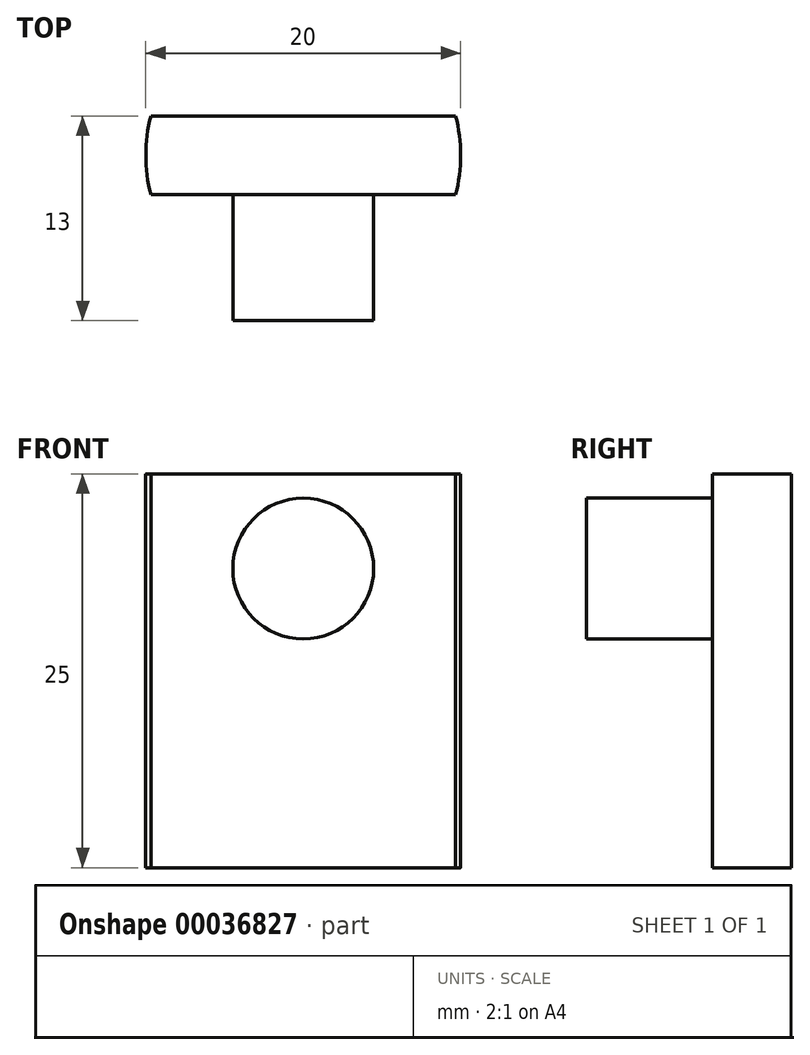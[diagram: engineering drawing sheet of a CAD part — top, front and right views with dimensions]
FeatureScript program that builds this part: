
annotation { "Feature Type Name" : "Feature", "Feature Type Description" : "" }
export const myFeature = defineFeature(function(context is Context, id is Id, definition is map)
    precondition{}
    {
        {
            var Q0;
            Q0=qCreatedBy(makeId("Top.planeOp"),FACE);
            var sketch = newSketch(context, id + "F0", { "sketchPlane" : qUnion([Q0])});
            skCircle(sketch, "E0", {"center": v(0, 0) * mm, "radius": 10 * mm});
            skLineSegment(sketch, "E1.rect.bottom", {"start": v(9.68, -2.5) * mm, "end": v(-9.68, -2.5) * mm});
            skLineSegment(sketch, "E1.rect.top", {"start": v(9.68, 2.5) * mm, "end": v(-9.68, 2.5) * mm});
            skSolve(sketch);
        }
        {
            var Q0;
            {var subQ1=sQuery(id+"F0.wireOp",EDGE,"E1.rect.bottom");Q0=makeQuery(id+"F0.imprint","IMPRINT",FACE,{"disambiguationData":[TD([[makeQuery(id+"F0.imprint","IMPRINT",EDGE,{"derivedFrom":subQ1}),-1.0]])]});}
            extrude(context, id + "F1", {"entities" : qUnion([Q0]), "depth" : 25 * mm});
        }
        {
            var Q0;
            Q0=makeQuery(id+"F1.opExtrude","SWEPT_FACE",FACE,{"disambiguationData":[OSD([sQuery(id+"F0.wireOp",EDGE,"E1.rect.bottom")])]});
            var sketch = newSketch(context, id + "F2", { "sketchPlane" : qUnion([Q0])});
            skCircle(sketch, "E2", {"center": v(0, 19) * mm, "radius": 4.47 * mm});
            skSolve(sketch);
        }
        {
            var Q0;
            Q0=makeQuery(id+"F2.imprint","IMPRINT",FACE,{"disambiguationData":[TD([[makeQuery(id+"F2.imprint","IMPRINT",EDGE,{"derivedFrom":sQuery(id+"F2.wireOp",EDGE,"E2")}),1.0]])]});
            extrude(context, id + "F3", {"entities" : qUnion([Q0]), "operationType" : NewBodyOperationType.ADD, "depth" : 8 * mm});
        }
    });
